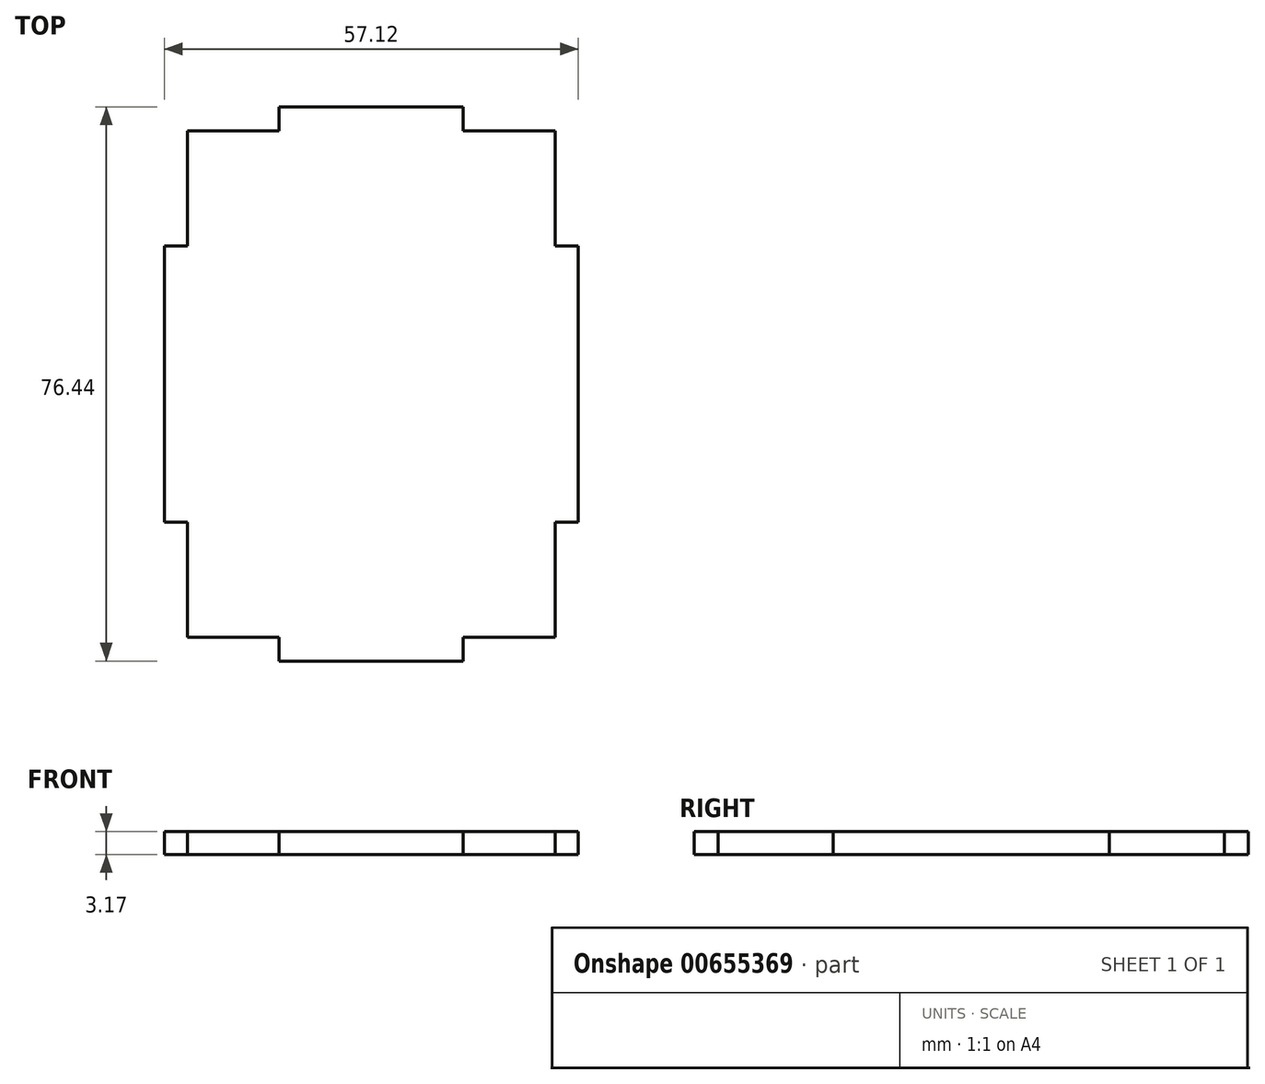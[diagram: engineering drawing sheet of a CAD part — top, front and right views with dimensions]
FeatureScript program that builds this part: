
annotation { "Feature Type Name" : "Feature", "Feature Type Description" : "" }
export const myFeature = defineFeature(function(context is Context, id is Id, definition is map)
    precondition{}
    {
        {
            var Q0;
            Q0=qCreatedBy(makeId("Top.planeOp"),FACE);
            var sketch = newSketch(context, id + "F0", { "sketchPlane" : qUnion([Q0])});
            skLineSegment(sketch, "E0.bottom", {"start": v(25.38, 34.92) * mm, "end": v(12.7, 34.92) * mm});
            skLineSegment(sketch, "E0.top", {"start": v(25.38, -34.92) * mm, "end": v(12.7, -34.92) * mm});
            skLineSegment(sketch, "E0.left", {"start": v(25.38, 34.92) * mm, "end": v(25.38, 19.05) * mm});
            skLineSegment(sketch, "E0.right", {"start": v(-25.38, 34.92) * mm, "end": v(-25.38, 19.05) * mm});
            skPoint(sketch, "E0.middle", {"position": v(0, 0) * mm});
            skLineSegment(sketch, "E1.bottom", {"start": v(28.56, 19.05) * mm, "end": v(25.38, 19.05) * mm});
            skLineSegment(sketch, "E1.top", {"start": v(28.56, -19.05) * mm, "end": v(25.38, -19.05) * mm});
            skLineSegment(sketch, "E1.left", {"start": v(28.56, 19.05) * mm, "end": v(28.56, -19.05) * mm});
            skPoint(sketch, "E1.middle", {"position": v(25.38, 0) * mm});
            skLineSegment(sketch, "E2.MirrorCS", {"start": v(-28.56, 19.05) * mm, "end": v(-28.56, -19.05) * mm});
            skLineSegment(sketch, "E3.MirrorCS", {"start": v(-28.56, 19.05) * mm, "end": v(-25.38, 19.05) * mm});
            skLineSegment(sketch, "E4.MirrorCS", {"start": v(-28.56, -19.05) * mm, "end": v(-25.38, -19.05) * mm});
            skLineSegment(sketch, "E5.bottom", {"start": v(12.7, 38.22) * mm, "end": v(-12.7, 38.22) * mm});
            skLineSegment(sketch, "E5.left", {"start": v(12.7, 38.22) * mm, "end": v(12.7, 34.92) * mm});
            skLineSegment(sketch, "E5.right", {"start": v(-12.7, 38.22) * mm, "end": v(-12.7, 34.92) * mm});
            skPoint(sketch, "E5.middle", {"position": v(0, 34.92) * mm});
            skLineSegment(sketch, "E6.MirrorCS", {"start": v(12.7, -38.22) * mm, "end": v(12.7, -34.92) * mm});
            skLineSegment(sketch, "E7.MirrorCS", {"start": v(12.7, -38.22) * mm, "end": v(-12.7, -38.22) * mm});
            skLineSegment(sketch, "E8.MirrorCS", {"start": v(-12.7, -38.22) * mm, "end": v(-12.7, -34.92) * mm});
            skPoint(sketch, "E9.orphan", {"position": v(-12.7, 31.63) * mm});
            skLineSegment(sketch, "E10.trimOffspring", {"start": v(-12.7, 34.92) * mm, "end": v(-25.38, 34.92) * mm});
            skPoint(sketch, "E11.orphan", {"position": v(12.7, 31.63) * mm});
            skLineSegment(sketch, "E12.trimOffspring", {"start": v(25.38, -19.05) * mm, "end": v(25.38, -34.92) * mm});
            skPoint(sketch, "E13.orphan", {"position": v(22.2, -19.05) * mm});
            skPoint(sketch, "E14.orphan", {"position": v(22.2, 19.05) * mm});
            skPoint(sketch, "E15.orphan", {"position": v(-22.2, 19.05) * mm});
            skPoint(sketch, "E16.MirrorCS.end.orphan", {"position": v(-22.2, -19.05) * mm});
            skLineSegment(sketch, "E17.trimOffspring", {"start": v(-25.38, -19.05) * mm, "end": v(-25.38, -34.92) * mm});
            skPoint(sketch, "E18.MirrorCS.end.orphan", {"position": v(-12.7, -31.63) * mm});
            skPoint(sketch, "E18.MirrorCS.start.orphan", {"position": v(12.7, -31.63) * mm});
            skLineSegment(sketch, "E19.trimOffspring", {"start": v(-12.7, -34.92) * mm, "end": v(-25.38, -34.92) * mm});
            skSolve(sketch);
        }
        {
            var Q0;
            Q0=makeQuery(id+"F0.imprint","IMPRINT",FACE,{"disambiguationData":[TD([[makeQuery(id+"F0.imprint","IMPRINT",EDGE,{"derivedFrom":sQuery(id+"F0.wireOp",EDGE,"E0.bottom")}),1.0]])]});
            extrude(context, id + "F1", {"entities" : qUnion([Q0]), "depth" : 3.17 * mm, "offsetDistance" : 25.4 * mm});
        }
    });
